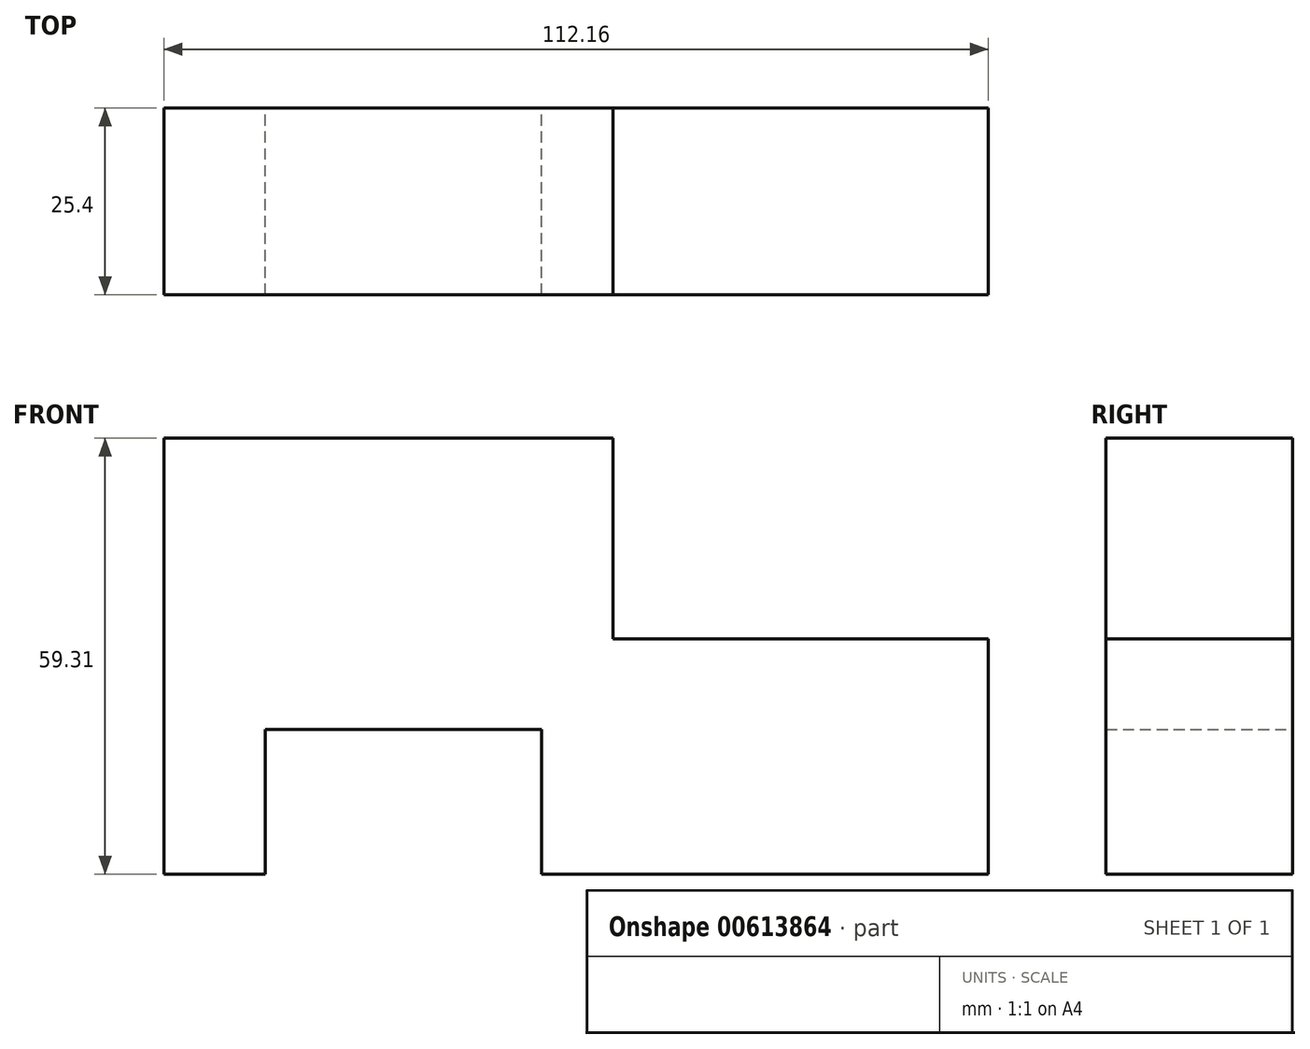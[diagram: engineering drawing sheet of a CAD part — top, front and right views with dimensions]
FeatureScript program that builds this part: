
annotation { "Feature Type Name" : "Feature", "Feature Type Description" : "" }
export const myFeature = defineFeature(function(context is Context, id is Id, definition is map)
    precondition{}
    {
        {
            var Q0;
            Q0=qCreatedBy(makeId("Front.planeOp"),FACE);
            var sketch = newSketch(context, id + "F0", { "sketchPlane" : qUnion([Q0])});
            skLineSegment(sketch, "E0", {"start": v(-66.8, 0) * mm, "end": v(-66.8, 59.31) * mm});
            skLineSegment(sketch, "E1", {"start": v(-66.8, 59.31) * mm, "end": v(-5.73, 59.31) * mm});
            skLineSegment(sketch, "E2", {"start": v(-5.73, 59.31) * mm, "end": v(-5.73, 32) * mm});
            skLineSegment(sketch, "E3", {"start": v(-5.73, 32) * mm, "end": v(45.36, 32) * mm});
            skLineSegment(sketch, "E4", {"start": v(45.36, 32) * mm, "end": v(45.36, 0) * mm});
            skLineSegment(sketch, "E5", {"start": v(45.36, 0) * mm, "end": v(-15.41, 0) * mm});
            skLineSegment(sketch, "E6", {"start": v(-15.41, 0) * mm, "end": v(-15.41, 19.67) * mm});
            skLineSegment(sketch, "E7", {"start": v(-15.41, 19.67) * mm, "end": v(-53, 19.67) * mm});
            skLineSegment(sketch, "E8", {"start": v(-53, 19.67) * mm, "end": v(-53, 0) * mm});
            skLineSegment(sketch, "E9", {"start": v(-53, 0) * mm, "end": v(-66.8, 0) * mm});
            skSolve(sketch);
        }
        {
            var Q0;
            Q0 = qSketchRegion(id + "F0", true);
            extrude(context, id + "F1", {"entities" : qUnion([Q0]), "depth" : 25.4 * mm, "offsetDistance" : 25.4 * mm});
        }
    });
